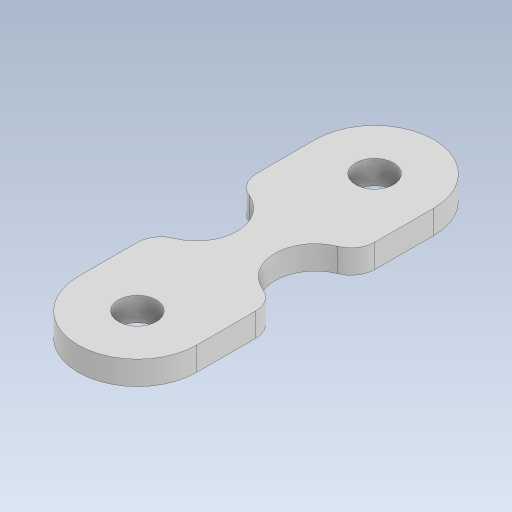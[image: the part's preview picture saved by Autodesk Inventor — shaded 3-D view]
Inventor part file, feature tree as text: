
AUTODESK INVENTOR PART (.ipt)
format: ipt  version: 2023.5 (Build 275446000, 446)  size: 118,272 bytes
history: native  units: mm
features: extrude x1, fillet x1, sketch x1
ambient origin geometry x8: Origin, YZ Plane, XZ Plane, XY Plane, X Axis, Y Axis, Z Axis, Center Point
bodies: Solid1 (feature_tree)
feature tree (3):
  extrude  "Extrusion1"  Depth=2.0mm
  fillet  "Fillet1"  Radius=20.0mm
  sketch  "Sketch1"  dims[d0=3.2mm d1=3.2mm d2=20.0mm d3=2.0mm d4=0.0mm d5=2.0mm]
